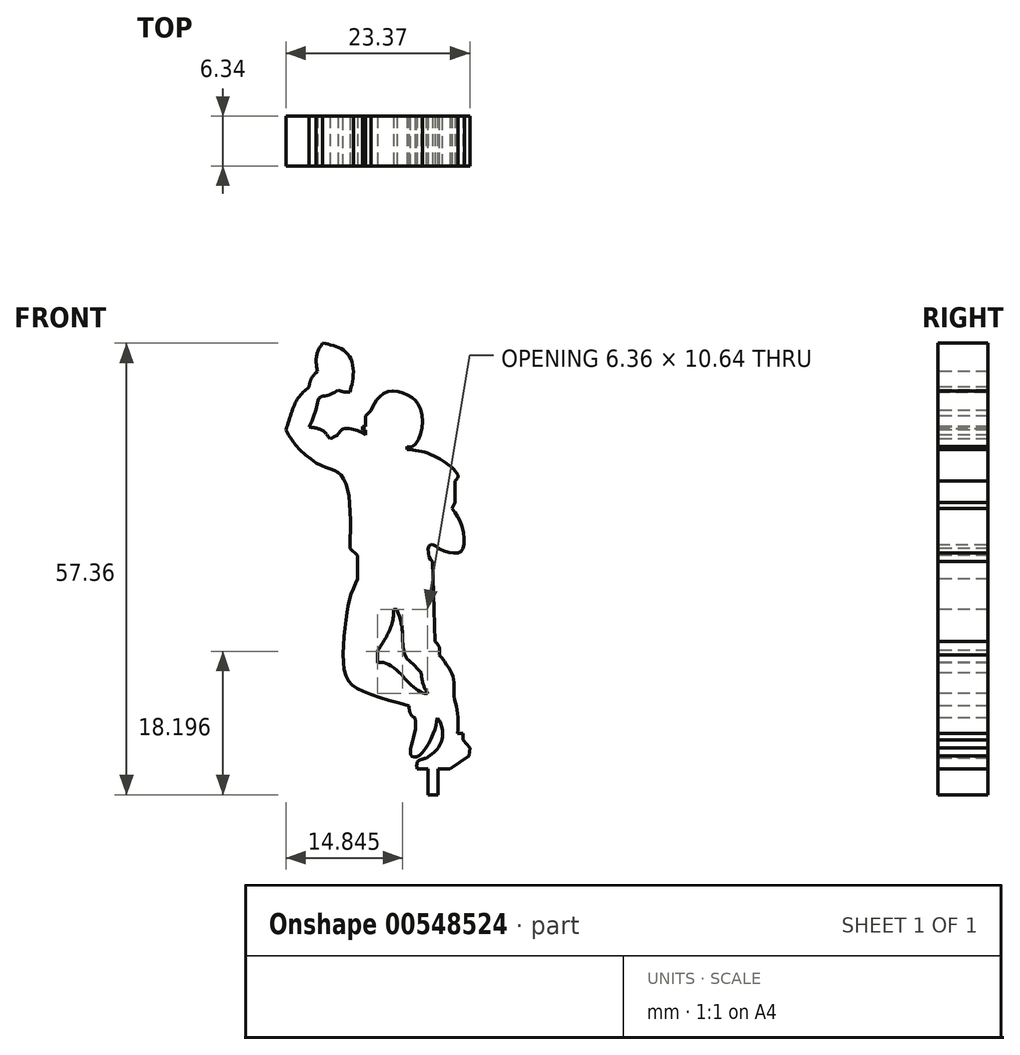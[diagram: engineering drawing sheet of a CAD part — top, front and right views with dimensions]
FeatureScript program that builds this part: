
annotation { "Feature Type Name" : "Feature", "Feature Type Description" : "" }
export const myFeature = defineFeature(function(context is Context, id is Id, definition is map)
    precondition{}
    {
        {
            var Q0;
            Q0=qCreatedBy(makeId("Front.planeOp"),FACE);
            var sketch = newSketch(context, id + "F0", { "sketchPlane" : qUnion([Q0])});
            skLineSegment(sketch, "E0", {"start": v(-7.94, 0) * mm, "end": v(-3.78, 0) * mm});
            skLineSegment(sketch, "E1", {"start": v(-3.78, 0) * mm, "end": v(-1.31, 1.7) * mm});
            skLineSegment(sketch, "E2", {"start": v(-1.31, 1.7) * mm, "end": v(-1.24, 2.7) * mm});
            skLineSegment(sketch, "E3", {"start": v(-1.24, 2.7) * mm, "end": v(-2.08, 3.7) * mm});
            skLineSegment(sketch, "E4", {"start": v(-2.08, 3.7) * mm, "end": v(-2.08, 4.54) * mm});
            skLineSegment(sketch, "E5", {"start": v(-2.08, 4.54) * mm, "end": v(-2.78, 4.54) * mm});
            skFitSpline(sketch, "E6", {"points": [v(-2.78, 4.54) * mm, v(-2.78, 7.09) * mm, v(-3.2, 9.13) * mm, v(-3.28, 11.1) * mm, v(-3.66, 12.45) * mm, v(-5.13, 14.53) * mm], "startDerivative": vector(0.75, 11.92) * mm, "endDerivative": vector(-7.74, 9.93) * mm});
            skFitSpline(sketch, "E7", {"points": [v(-5.13, 14.53) * mm, v(-5.13, 15.5) * mm, v(-5.63, 16.22) * mm], "startDerivative": vector(0.26, 1.99) * mm, "endDerivative": vector(-1.27, 1.4) * mm});
            skLineSegment(sketch, "E8", {"start": v(-5.63, 16.22) * mm, "end": v(-5.98, 26.4) * mm});
            skFitSpline(sketch, "E9", {"points": [v(-5.98, 26.4) * mm, v(-6.4, 26.98) * mm, v(-6.44, 28.33) * mm, v(-5.98, 28.52) * mm, v(-5.05, 27.98) * mm, v(-2.97, 27.44) * mm, v(-2.05, 28.13) * mm, v(-2.31, 31.03) * mm, v(-3.47, 33.1) * mm], "startDerivative": vector(-5.34, 4.93) * mm, "endDerivative": vector(-7.93, 11.34) * mm});
            skLineSegment(sketch, "E10", {"start": v(-3.47, 33.1) * mm, "end": v(-3.11, 33.89) * mm});
            skLineSegment(sketch, "E11", {"start": v(-3.11, 33.89) * mm, "end": v(-3.11, 36.64) * mm});
            skFitSpline(sketch, "E12", {"points": [v(-3.11, 36.64) * mm, v(-2.75, 37.23) * mm, v(-3.98, 38.7) * mm, v(-6.83, 40.21) * mm, v(-9.2, 40.63) * mm], "startDerivative": vector(3.76, 3.56) * mm, "endDerivative": vector(-8.35, 0.8) * mm});
            skLineSegment(sketch, "E13", {"start": v(-9.2, 40.63) * mm, "end": v(-9.2, 41) * mm});
            skFitSpline(sketch, "E14", {"points": [v(-9.2, 41) * mm, v(-8.57, 41) * mm, v(-7.38, 42.92) * mm, v(-7.74, 46.26) * mm, v(-9.2, 47.55) * mm, v(-11.55, 48) * mm, v(-13.1, 46.81) * mm, v(-13.8, 45.53) * mm], "startDerivative": vector(7.43, -1.98) * mm, "endDerivative": vector(-4.52, -10.18) * mm});
            skLineSegment(sketch, "E15", {"start": v(-13.8, 45.53) * mm, "end": v(-14.48, 44.84) * mm});
            skLineSegment(sketch, "E16", {"start": v(-14.48, 44.84) * mm, "end": v(-14.48, 43.56) * mm});
            skLineSegment(sketch, "E17", {"start": v(-14.48, 43.56) * mm, "end": v(-14.9, 43.56) * mm});
            skLineSegment(sketch, "E18", {"start": v(-14.9, 43.56) * mm, "end": v(-14.9, 43.1) * mm});
            skLineSegment(sketch, "E19", {"start": v(-14.9, 43.1) * mm, "end": v(-14.48, 43.1) * mm});
            skLineSegment(sketch, "E20", {"start": v(-14.48, 43.1) * mm, "end": v(-14.48, 42.46) * mm});
            skFitSpline(sketch, "E21", {"points": [v(-14.48, 42.46) * mm, v(-15.76, 43.1) * mm, v(-17.46, 43.15) * mm, v(-18.06, 42.46) * mm, v(-19.02, 41.96) * mm, v(-19.02, 41.86) * mm], "startDerivative": vector(-4.53, 2.9) * mm, "endDerivative": vector(0.64, -1.4) * mm});
            skFitSpline(sketch, "E22", {"points": [v(-19.02, 41.96) * mm, v(-19.94, 43) * mm, v(-21.63, 43.47) * mm], "startDerivative": vector(-1.65, 2.56) * mm, "endDerivative": vector(-3.54, 0.5) * mm});
            skFitSpline(sketch, "E23", {"points": [v(-21.63, 43.47) * mm, v(-20.71, 45.9) * mm, v(-20.44, 47.04) * mm, v(-20.07, 47.32) * mm, v(-19.02, 47.6) * mm, v(-17.96, 48.14) * mm], "startDerivative": vector(3.8, 8.76) * mm, "endDerivative": vector(5.07, 3.16) * mm});
            skFitSpline(sketch, "E24", {"points": [v(-17.96, 48.14) * mm, v(-17.25, 47.93) * mm, v(-16.48, 47.93) * mm], "startDerivative": vector(1.42, -0.52) * mm, "endDerivative": vector(1.54, 0.1) * mm});
            skFitSpline(sketch, "E25", {"points": [v(-16.48, 47.93) * mm, v(-16.13, 49.37) * mm, v(-16.16, 51.57) * mm, v(-17.06, 53.05) * mm, v(-18.47, 53.78) * mm, v(-19.92, 54.1) * mm], "startDerivative": vector(2.14, 7.06) * mm, "endDerivative": vector(-7.7, 1.4) * mm});
            skFitSpline(sketch, "E26", {"points": [v(-19.92, 54.1) * mm, v(-20.4, 53.35) * mm, v(-20.76, 52.06) * mm, v(-20.57, 50.54) * mm], "startDerivative": vector(-1.8, -2.45) * mm, "endDerivative": vector(0.89, -4.15) * mm});
            skFitSpline(sketch, "E27", {"points": [v(-20.57, 50.54) * mm, v(-21.36, 49.64) * mm, v(-21.66, 48.52) * mm], "startDerivative": vector(-1.81, -1.66) * mm, "endDerivative": vector(-0.37, -2.37) * mm});
            skFitSpline(sketch, "E28", {"points": [v(-21.66, 48.52) * mm, v(-22.86, 47.4) * mm, v(-23.76, 45.66) * mm, v(-24.6, 43.07) * mm], "startDerivative": vector(-4.35, -3.45) * mm, "endDerivative": vector(-2.15, -7.08) * mm});
            skFitSpline(sketch, "E29", {"points": [v(-24.6, 43.07) * mm, v(-23.22, 41.03) * mm, v(-20.76, 38.93) * mm, v(-19.05, 38.2) * mm, v(-17.96, 37.67) * mm, v(-17.11, 36.56) * mm, v(-16.48, 33.62) * mm, v(-16.48, 28.04) * mm], "startDerivative": vector(8.43, -14.32) * mm, "endDerivative": vector(-0.93, -27.85) * mm});
            skLineSegment(sketch, "E30", {"start": v(-16.48, 28.04) * mm, "end": v(-15.48, 27.17) * mm});
            skLineSegment(sketch, "E31", {"start": v(-15.48, 27.17) * mm, "end": v(-15.48, 24.18) * mm});
            skFitSpline(sketch, "E32", {"points": [v(-15.48, 24.18) * mm, v(-16.42, 21.89) * mm, v(-17.11, 17.76) * mm, v(-17.11, 12.26) * mm, v(-15.48, 10.24) * mm, v(-8.97, 8.04) * mm], "startDerivative": vector(-6.64, -13.9) * mm, "endDerivative": vector(29.46, -8.04) * mm});
            skFitSpline(sketch, "E33", {"points": [v(-8.97, 8.04) * mm, v(-8.73, 6.97) * mm, v(-8.19, 6.5) * mm], "startDerivative": vector(0.22, -2.2) * mm, "endDerivative": vector(1.4, -0.84) * mm});
            skFitSpline(sketch, "E34", {"points": [v(-8.19, 6.5) * mm, v(-8.19, 4.87) * mm, v(-8.65, 3.02) * mm, v(-8.76, 1.87) * mm, v(-8.4, 1.54) * mm, v(-7.37, 1.98) * mm, v(-5.82, 4.65) * mm, v(-5.35, 6.5) * mm], "startDerivative": vector(0.8, -10.8) * mm, "endDerivative": vector(1.88, 10.6) * mm});
            skPoint(sketch, "E35.2.internal.snap0", {"position": v(-1.66, 3.2) * mm});
            skFitSpline(sketch, "E35", {"points": [v(-5.35, 6.5) * mm, v(-4.81, 5.46) * mm, v(-4.97, 3.2) * mm, v(-6.78, 1.38) * mm], "startDerivative": vector(2.43, -3.43) * mm, "endDerivative": vector(-5.73, -4.15) * mm});
            skFitSpline(sketch, "E36", {"points": [v(-6.78, 1.38) * mm, v(-7.86, 0.95) * mm, v(-7.94, 0) * mm], "startDerivative": vector(-2.55, -0.5) * mm, "endDerivative": vector(0.27, -2.29) * mm});
            skFitSpline(sketch, "E37", {"points": [v(-10.9, 20.26) * mm, v(-11.06, 18.76) * mm, v(-11.87, 16.76) * mm, v(-12.94, 15.1) * mm], "startDerivative": vector(-0.14, -4.83) * mm, "endDerivative": vector(-3.26, -4.6) * mm});
            skLineSegment(sketch, "E38", {"start": v(-12.94, 15.1) * mm, "end": v(-12.94, 13.48) * mm});
            skLineSegment(sketch, "E39", {"start": v(-10.9, 20.26) * mm, "end": v(-10.48, 20.26) * mm});
            skFitSpline(sketch, "E40", {"points": [v(-12.94, 13.48) * mm, v(-11.94, 13.48) * mm, v(-10.05, 12.13) * mm, v(-8.78, 10.78) * mm, v(-7.24, 9.7) * mm, v(-6.58, 9.63) * mm], "startDerivative": vector(5.62, 1.13) * mm, "endDerivative": vector(4.41, 0.22) * mm});
            skFitSpline(sketch, "E41", {"points": [v(-6.58, 9.63) * mm, v(-7.12, 10.67) * mm, v(-7.41, 12.2) * mm, v(-7.4, 12.25) * mm], "startDerivative": vector(-1.35, 1.9) * mm, "endDerivative": vector(0.46, 0.22) * mm});
            skFitSpline(sketch, "E42", {"points": [v(-7.4, 12.25) * mm, v(-8.63, 13.48) * mm, v(-9.44, 14.4) * mm, v(-9.78, 16.49) * mm, v(-9.86, 18.03) * mm, v(-10.48, 20.26) * mm], "startDerivative": vector(-6.4, 6.7) * mm, "endDerivative": vector(-3.38, 10.38) * mm});
            skLineSegment(sketch, "E43", {"start": v(-7.94, 0) * mm, "end": v(-6.56, 0) * mm});
            skLineSegment(sketch, "E44", {"start": v(-6.56, 0) * mm, "end": v(-6.56, -3.25) * mm});
            skLineSegment(sketch, "E45", {"start": v(-6.56, -3.25) * mm, "end": v(-5.28, -3.25) * mm});
            skLineSegment(sketch, "E46", {"start": v(-5.28, -3.25) * mm, "end": v(-5.28, 0) * mm});
            skLineSegment(sketch, "E47", {"start": v(-5.28, 0) * mm, "end": v(-3.78, 0) * mm});
            skSolve(sketch);
        }
        {
            var Q0;
            Q0=makeQuery(id+"F0.imprint","IMPRINT",FACE,{"disambiguationData":[TD([[makeQuery(id+"F0.imprint","IMPRINT",EDGE,{"derivedFrom":sQuery(id+"F0.wireOp",EDGE,"E0")}),1.0]])]});
            var Q1;
            Q1=makeQuery(id+"F0.imprint","IMPRINT",FACE,{"disambiguationData":[TD([[makeQuery(id+"F0.imprint","IMPRINT",EDGE,{"derivedFrom":sQuery(id+"F0.wireOp",EDGE,"E0")}),-1.0]])]});
            extrude(context, id + "F1", {"entities" : qUnion([Q0, Q1]), "oppositeDirection" : true, "depth" : 6.34 * mm, "offsetDistance" : 25 * mm});
        }
    });
